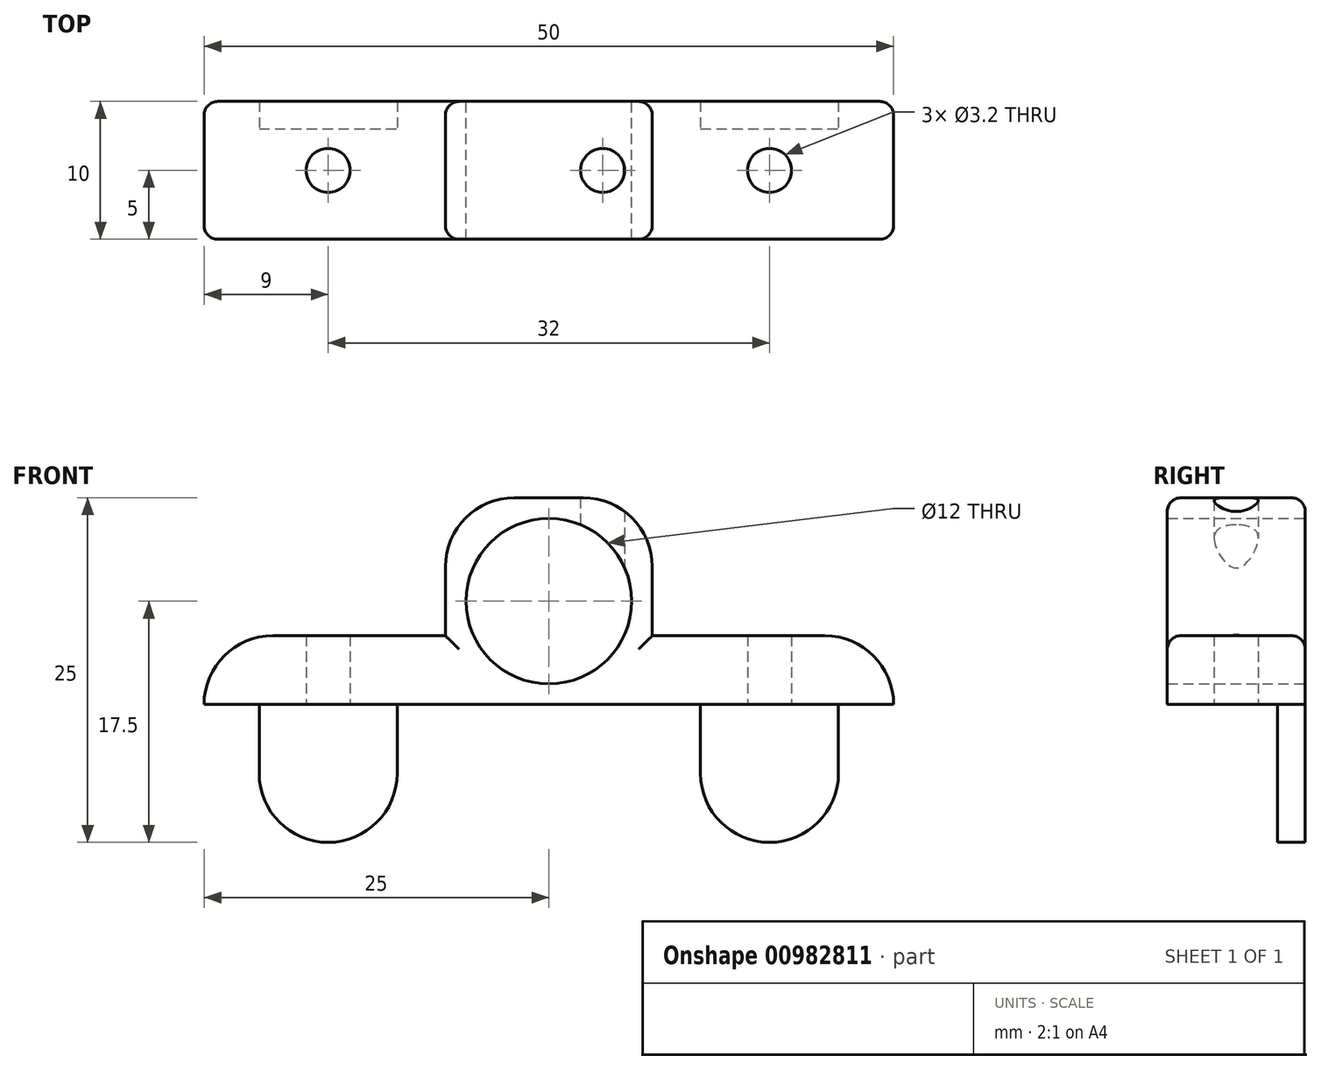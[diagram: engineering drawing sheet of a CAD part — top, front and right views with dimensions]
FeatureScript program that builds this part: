
annotation { "Feature Type Name" : "Feature", "Feature Type Description" : "" }
export const myFeature = defineFeature(function(context is Context, id is Id, definition is map)
    precondition{}
    {
        {
            var Q0;
            Q0=qCreatedBy(makeId("Top.planeOp"),FACE);
            var sketch = newSketch(context, id + "F0", { "sketchPlane" : qUnion([Q0])});
            skLineSegment(sketch, "E0.bottom", {"start": v(25, -5) * mm, "end": v(-25, -5) * mm});
            skLineSegment(sketch, "E0.top", {"start": v(25, 5) * mm, "end": v(-25, 5) * mm});
            skLineSegment(sketch, "E0.left", {"start": v(25, -5) * mm, "end": v(25, 5) * mm});
            skLineSegment(sketch, "E0.right", {"start": v(-25, -5) * mm, "end": v(-25, 5) * mm});
            skPoint(sketch, "E0.middle", {"position": v(0, 0) * mm});
            skCircle(sketch, "E1", {"center": v(-16, 0) * mm, "radius": 1.6 * mm});
            skLineSegment(sketch, "E2", {"start": v(-16, 0) * mm, "end": v(0, 0) * mm, "construction": true});
            skLineSegment(sketch, "E3", {"start": v(0, 5) * mm, "end": v(0, -5) * mm, "construction": true});
            skCircle(sketch, "E4.MirrorC", {"center": v(16, 0) * mm, "radius": 1.6 * mm});
            skSolve(sketch);
        }
        {
            var Q0;
            Q0=makeQuery(id+"F0.imprint","IMPRINT",FACE,{"disambiguationData":[TD([[makeQuery(id+"F0.imprint","IMPRINT",EDGE,{"derivedFrom":sQuery(id+"F0.wireOp",EDGE,"E0.bottom")}),-1.0]])]});
            extrude(context, id + "F1", {"entities" : qUnion([Q0]), "depth" : 5 * mm, "offsetDistance" : 25 * mm});
        }
        {
            var Q0;
            Q0=makeQuery(id+"F1.opExtrude","CAP_FACE",FACE,{"disambiguationData":[OSD([sQuery(id+"F0.wireOp",EDGE,"E0.bottom"),sQuery(id+"F0.wireOp",EDGE,"E0.top"),sQuery(id+"F0.wireOp",EDGE,"E0.left"),sQuery(id+"F0.wireOp",EDGE,"E0.right"),sQuery(id+"F0.wireOp",EDGE,"E1"),sQuery(id+"F0.wireOp",EDGE,"E4.MirrorC")])],"isStart":false});
            var sketch = newSketch(context, id + "F2", { "sketchPlane" : qUnion([Q0])});
            skLineSegment(sketch, "E5.bottom", {"start": v(7.5, -5) * mm, "end": v(-7.5, -5) * mm});
            skLineSegment(sketch, "E5.top", {"start": v(7.5, 5) * mm, "end": v(-7.5, 5) * mm});
            skLineSegment(sketch, "E5.left", {"start": v(7.5, -5) * mm, "end": v(7.5, 5) * mm});
            skLineSegment(sketch, "E5.right", {"start": v(-7.5, -5) * mm, "end": v(-7.5, 5) * mm});
            skPoint(sketch, "E5.middle", {"position": v(0, 0) * mm});
            skCircle(sketch, "E6", {"center": v(-3.9, 0) * mm, "radius": 1.6 * mm});
            skPoint(sketch, "E6.centerSnap0", {"position": v(-7.5, 0) * mm});
            skLineSegment(sketch, "E7", {"start": v(-7.5, 0) * mm, "end": v(-5.5, 0) * mm, "construction": true});
            skCircle(sketch, "E8.MirrorC", {"center": v(3.9, 0) * mm, "radius": 1.6 * mm});
            skSolve(sketch);
        }
        {
            var Q0;
            Q0=makeQuery(id+"F2.imprint","IMPRINT",FACE,{"disambiguationData":[TD([[makeQuery(id+"F2.imprint","IMPRINT",EDGE,{"derivedFrom":sQuery(id+"F2.wireOp",EDGE,"E5.bottom")}),-1.0]])]});
            var Q1;
            Q1=makeQuery(id+"F2.imprint","IMPRINT",FACE,{"disambiguationData":[TD([[makeQuery(id+"F2.imprint","IMPRINT",EDGE,{"derivedFrom":sQuery(id+"F2.wireOp",EDGE,"E8.MirrorC")}),-1.0]])]});
            var Q2;
            Q2=makeQuery(id+"F2.imprint","IMPRINT",FACE,{"disambiguationData":[TD([[makeQuery(id+"F2.imprint","IMPRINT",EDGE,{"derivedFrom":sQuery(id+"F2.wireOp",EDGE,"E6")}),1.0]])]});
            extrude(context, id + "F3", {"entities" : qUnion([Q0, Q1, Q2]), "operationType" : NewBodyOperationType.ADD, "depth" : 10 * mm, "offsetDistance" : 25 * mm});
        }
        {
            var Q0;
            Q0=makeQuery(id+"F3.boolean.opBoolean","MERGE",FACE,{"derivedFrom":[makeQuery(id+"F1.opExtrude","SWEPT_FACE",FACE,{"disambiguationData":[OSD([sQuery(id+"F0.wireOp",EDGE,"E0.top")])]}),makeQuery(id+"F3.opExtrude","SWEPT_FACE",FACE,{"disambiguationData":[OSD([sQuery(id+"F2.wireOp",EDGE,"E5.top")])]})]});
            var sketch = newSketch(context, id + "F4", { "sketchPlane" : qUnion([Q0])});
            skCircle(sketch, "E9", {"center": v(0, 7.5) * mm, "radius": 6 * mm});
            skLineSegment(sketch, "E10", {"start": v(0, 7.5) * mm, "end": v(0, 0) * mm, "construction": true});
            skSolve(sketch);
        }
        {
            var Q0;
            Q0=makeQuery(id+"F3.opExtrude","CAP_EDGE",EDGE,{"disambiguationData":[OSD([sQuery(id+"F2.wireOp",EDGE,"E5.left")])],"isStart":false});
            var Q1;
            Q1=makeQuery(id+"F3.opExtrude","CAP_EDGE",EDGE,{"disambiguationData":[OSD([sQuery(id+"F2.wireOp",EDGE,"E5.right")])],"isStart":false});
            fillet(context, id + "F5", {"entities" : qUnion([Q0, Q1]), "radius" : 5 * mm, "tangentPropagation" : true, "allowEdgeOverflow" : false});
        }
        {
            var Q0;
            Q0=makeQuery(id+"F1.opExtrude","CAP_EDGE",EDGE,{"disambiguationData":[OSD([sQuery(id+"F0.wireOp",EDGE,"E0.right")])],"isStart":false});
            var Q1;
            Q1=makeQuery(id+"F1.opExtrude","CAP_EDGE",EDGE,{"disambiguationData":[OSD([sQuery(id+"F0.wireOp",EDGE,"E0.left")])],"isStart":false});
            fillet(context, id + "F6", {"entities" : qUnion([Q0, Q1]), "radius" : 5 * mm, "tangentPropagation" : true, "allowEdgeOverflow" : false});
        }
        {
            var Q0;
            Q0=makeQuery(id+"F4.imprint","IMPRINT",FACE,{"disambiguationData":[TD([[makeQuery(id+"F4.imprint","IMPRINT",EDGE,{"derivedFrom":sQuery(id+"F4.wireOp",EDGE,"E9")}),1.0]])]});
            extrude(context, id + "F7", {"entities" : qUnion([Q0]), "operationType" : NewBodyOperationType.REMOVE, "oppositeDirection" : true, "depth" : 25 * mm, "offsetDistance" : 25 * mm});
        }
        {
            var Q0;
            Q0=makeQuery(id+"F6.opFillet","BLEND_EDGE",EDGE,{"blendedFrom":[makeQuery(id+"F1.opExtrude","CAP_EDGE",EDGE,{"disambiguationData":[OSD([sQuery(id+"F0.wireOp",EDGE,"E0.left")])],"isStart":false}),makeQuery(id+"F3.boolean.opBoolean","MERGE",FACE,{"derivedFrom":[makeQuery(id+"F1.opExtrude","SWEPT_FACE",FACE,{"disambiguationData":[OSD([sQuery(id+"F0.wireOp",EDGE,"E0.bottom")])]}),makeQuery(id+"F3.opExtrude","SWEPT_FACE",FACE,{"disambiguationData":[OSD([sQuery(id+"F2.wireOp",EDGE,"E5.bottom")])]})]})],"blendedInto":[makeQuery(id+"F3.boolean.opBoolean","MERGE",FACE,{"derivedFrom":[makeQuery(id+"F1.opExtrude","SWEPT_FACE",FACE,{"disambiguationData":[OSD([sQuery(id+"F0.wireOp",EDGE,"E0.bottom")])]}),makeQuery(id+"F3.opExtrude","SWEPT_FACE",FACE,{"disambiguationData":[OSD([sQuery(id+"F2.wireOp",EDGE,"E5.bottom")])]})]})]});
            var Q1;
            {var subQ0=sQuery(id+"F0.wireOp",EDGE,"E0.left");var subQ1=sQuery(id+"F0.wireOp",EDGE,"E0.bottom");Q1=makeQuery(id+"F3.boolean.opBoolean","SPLIT",EDGE,{"disambiguationData":[TD([makeQuery(id+"F1.opExtrude","SWEPT_FACE",FACE,{"disambiguationData":[OSD([subQ0])]})])],"derivedFrom":makeQuery(id+"F1.opExtrude","CAP_EDGE",EDGE,{"disambiguationData":[OSD([subQ1])],"isStart":false})});}
            var Q2;
            Q2=makeQuery(id+"F3.opExtrude","SWEPT_EDGE",EDGE,{"disambiguationData":[OSD([sQuery(id+"F0.wireOp",EDGE,"E0.bottom"),sQuery(id+"F2.wireOp",EDGE,"E5.bottom"),sQuery(id+"F2.wireOp",EDGE,"E5.left")])]});
            var Q3;
            Q3=makeQuery(id+"F5.opFillet","BLEND_EDGE",EDGE,{"blendedFrom":[makeQuery(id+"F3.opExtrude","CAP_EDGE",EDGE,{"disambiguationData":[OSD([sQuery(id+"F2.wireOp",EDGE,"E5.left")])],"isStart":false}),makeQuery(id+"F3.boolean.opBoolean","MERGE",FACE,{"derivedFrom":[makeQuery(id+"F1.opExtrude","SWEPT_FACE",FACE,{"disambiguationData":[OSD([sQuery(id+"F0.wireOp",EDGE,"E0.bottom")])]}),makeQuery(id+"F3.opExtrude","SWEPT_FACE",FACE,{"disambiguationData":[OSD([sQuery(id+"F2.wireOp",EDGE,"E5.bottom")])]})]})],"blendedInto":[makeQuery(id+"F3.boolean.opBoolean","MERGE",FACE,{"derivedFrom":[makeQuery(id+"F1.opExtrude","SWEPT_FACE",FACE,{"disambiguationData":[OSD([sQuery(id+"F0.wireOp",EDGE,"E0.bottom")])]}),makeQuery(id+"F3.opExtrude","SWEPT_FACE",FACE,{"disambiguationData":[OSD([sQuery(id+"F2.wireOp",EDGE,"E5.bottom")])]})]})]});
            var Q4;
            Q4=makeQuery(id+"F3.opExtrude","CAP_EDGE",EDGE,{"disambiguationData":[OSD([sQuery(id+"F2.wireOp",EDGE,"E5.bottom")])],"isStart":false});
            var Q5;
            Q5=makeQuery(id+"F5.opFillet","BLEND_EDGE",EDGE,{"blendedFrom":[makeQuery(id+"F3.opExtrude","CAP_EDGE",EDGE,{"disambiguationData":[OSD([sQuery(id+"F2.wireOp",EDGE,"E5.right")])],"isStart":false}),makeQuery(id+"F3.boolean.opBoolean","MERGE",FACE,{"derivedFrom":[makeQuery(id+"F1.opExtrude","SWEPT_FACE",FACE,{"disambiguationData":[OSD([sQuery(id+"F0.wireOp",EDGE,"E0.bottom")])]}),makeQuery(id+"F3.opExtrude","SWEPT_FACE",FACE,{"disambiguationData":[OSD([sQuery(id+"F2.wireOp",EDGE,"E5.bottom")])]})]})],"blendedInto":[makeQuery(id+"F3.boolean.opBoolean","MERGE",FACE,{"derivedFrom":[makeQuery(id+"F1.opExtrude","SWEPT_FACE",FACE,{"disambiguationData":[OSD([sQuery(id+"F0.wireOp",EDGE,"E0.bottom")])]}),makeQuery(id+"F3.opExtrude","SWEPT_FACE",FACE,{"disambiguationData":[OSD([sQuery(id+"F2.wireOp",EDGE,"E5.bottom")])]})]})]});
            var Q6;
            Q6=makeQuery(id+"F3.opExtrude","SWEPT_EDGE",EDGE,{"disambiguationData":[OSD([sQuery(id+"F0.wireOp",EDGE,"E0.bottom"),sQuery(id+"F2.wireOp",EDGE,"E5.bottom"),sQuery(id+"F2.wireOp",EDGE,"E5.right")])]});
            var Q7;
            {var subQ0=sQuery(id+"F0.wireOp",EDGE,"E0.right");var subQ1=sQuery(id+"F0.wireOp",EDGE,"E0.bottom");Q7=makeQuery(id+"F3.boolean.opBoolean","SPLIT",EDGE,{"disambiguationData":[TD([makeQuery(id+"F1.opExtrude","SWEPT_FACE",FACE,{"disambiguationData":[OSD([subQ0])]})])],"derivedFrom":makeQuery(id+"F1.opExtrude","CAP_EDGE",EDGE,{"disambiguationData":[OSD([subQ1])],"isStart":false})});}
            var Q8;
            Q8=makeQuery(id+"F6.opFillet","BLEND_EDGE",EDGE,{"blendedFrom":[makeQuery(id+"F1.opExtrude","CAP_EDGE",EDGE,{"disambiguationData":[OSD([sQuery(id+"F0.wireOp",EDGE,"E0.right")])],"isStart":false}),makeQuery(id+"F3.boolean.opBoolean","MERGE",FACE,{"derivedFrom":[makeQuery(id+"F1.opExtrude","SWEPT_FACE",FACE,{"disambiguationData":[OSD([sQuery(id+"F0.wireOp",EDGE,"E0.bottom")])]}),makeQuery(id+"F3.opExtrude","SWEPT_FACE",FACE,{"disambiguationData":[OSD([sQuery(id+"F2.wireOp",EDGE,"E5.bottom")])]})]})],"blendedInto":[makeQuery(id+"F3.boolean.opBoolean","MERGE",FACE,{"derivedFrom":[makeQuery(id+"F1.opExtrude","SWEPT_FACE",FACE,{"disambiguationData":[OSD([sQuery(id+"F0.wireOp",EDGE,"E0.bottom")])]}),makeQuery(id+"F3.opExtrude","SWEPT_FACE",FACE,{"disambiguationData":[OSD([sQuery(id+"F2.wireOp",EDGE,"E5.bottom")])]})]})]});
            var Q9;
            {var subQ0=sQuery(id+"F0.wireOp",EDGE,"E0.right");var subQ1=sQuery(id+"F0.wireOp",EDGE,"E0.top");Q9=makeQuery(id+"F3.boolean.opBoolean","SPLIT",EDGE,{"disambiguationData":[TD([makeQuery(id+"F1.opExtrude","SWEPT_FACE",FACE,{"disambiguationData":[OSD([subQ0])]})])],"derivedFrom":makeQuery(id+"F1.opExtrude","CAP_EDGE",EDGE,{"disambiguationData":[OSD([subQ1])],"isStart":false})});}
            var Q10;
            Q10=makeQuery(id+"F3.opExtrude","CAP_EDGE",EDGE,{"disambiguationData":[OSD([sQuery(id+"F2.wireOp",EDGE,"E5.top")])],"isStart":false});
            var Q11;
            Q11=makeQuery(id+"F5.opFillet","BLEND_EDGE",EDGE,{"blendedFrom":[makeQuery(id+"F3.opExtrude","CAP_EDGE",EDGE,{"disambiguationData":[OSD([sQuery(id+"F2.wireOp",EDGE,"E5.left")])],"isStart":false}),makeQuery(id+"F3.boolean.opBoolean","MERGE",FACE,{"derivedFrom":[makeQuery(id+"F1.opExtrude","SWEPT_FACE",FACE,{"disambiguationData":[OSD([sQuery(id+"F0.wireOp",EDGE,"E0.top")])]}),makeQuery(id+"F3.opExtrude","SWEPT_FACE",FACE,{"disambiguationData":[OSD([sQuery(id+"F2.wireOp",EDGE,"E5.top")])]})]})],"blendedInto":[makeQuery(id+"F3.boolean.opBoolean","MERGE",FACE,{"derivedFrom":[makeQuery(id+"F1.opExtrude","SWEPT_FACE",FACE,{"disambiguationData":[OSD([sQuery(id+"F0.wireOp",EDGE,"E0.top")])]}),makeQuery(id+"F3.opExtrude","SWEPT_FACE",FACE,{"disambiguationData":[OSD([sQuery(id+"F2.wireOp",EDGE,"E5.top")])]})]})]});
            var Q12;
            {var subQ0=sQuery(id+"F0.wireOp",EDGE,"E0.left");var subQ1=sQuery(id+"F0.wireOp",EDGE,"E0.top");Q12=makeQuery(id+"F3.boolean.opBoolean","SPLIT",EDGE,{"disambiguationData":[TD([makeQuery(id+"F1.opExtrude","SWEPT_FACE",FACE,{"disambiguationData":[OSD([subQ0])]})])],"derivedFrom":makeQuery(id+"F1.opExtrude","CAP_EDGE",EDGE,{"disambiguationData":[OSD([subQ1])],"isStart":false})});}
            var Q13;
            Q13=makeQuery(id+"F6.opFillet","BLEND_EDGE",EDGE,{"blendedFrom":[makeQuery(id+"F1.opExtrude","CAP_EDGE",EDGE,{"disambiguationData":[OSD([sQuery(id+"F0.wireOp",EDGE,"E0.left")])],"isStart":false}),makeQuery(id+"F3.boolean.opBoolean","MERGE",FACE,{"derivedFrom":[makeQuery(id+"F1.opExtrude","SWEPT_FACE",FACE,{"disambiguationData":[OSD([sQuery(id+"F0.wireOp",EDGE,"E0.top")])]}),makeQuery(id+"F3.opExtrude","SWEPT_FACE",FACE,{"disambiguationData":[OSD([sQuery(id+"F2.wireOp",EDGE,"E5.top")])]})]})],"blendedInto":[makeQuery(id+"F3.boolean.opBoolean","MERGE",FACE,{"derivedFrom":[makeQuery(id+"F1.opExtrude","SWEPT_FACE",FACE,{"disambiguationData":[OSD([sQuery(id+"F0.wireOp",EDGE,"E0.top")])]}),makeQuery(id+"F3.opExtrude","SWEPT_FACE",FACE,{"disambiguationData":[OSD([sQuery(id+"F2.wireOp",EDGE,"E5.top")])]})]})]});
            var Q14;
            Q14=makeQuery(id+"F3.opExtrude","SWEPT_EDGE",EDGE,{"disambiguationData":[OSD([sQuery(id+"F0.wireOp",EDGE,"E0.top"),sQuery(id+"F2.wireOp",EDGE,"E5.top"),sQuery(id+"F2.wireOp",EDGE,"E5.left")])]});
            var Q15;
            Q15=makeQuery(id+"F5.opFillet","BLEND_EDGE",EDGE,{"blendedFrom":[makeQuery(id+"F3.opExtrude","CAP_EDGE",EDGE,{"disambiguationData":[OSD([sQuery(id+"F2.wireOp",EDGE,"E5.right")])],"isStart":false}),makeQuery(id+"F3.boolean.opBoolean","MERGE",FACE,{"derivedFrom":[makeQuery(id+"F1.opExtrude","SWEPT_FACE",FACE,{"disambiguationData":[OSD([sQuery(id+"F0.wireOp",EDGE,"E0.top")])]}),makeQuery(id+"F3.opExtrude","SWEPT_FACE",FACE,{"disambiguationData":[OSD([sQuery(id+"F2.wireOp",EDGE,"E5.top")])]})]})],"blendedInto":[makeQuery(id+"F3.boolean.opBoolean","MERGE",FACE,{"derivedFrom":[makeQuery(id+"F1.opExtrude","SWEPT_FACE",FACE,{"disambiguationData":[OSD([sQuery(id+"F0.wireOp",EDGE,"E0.top")])]}),makeQuery(id+"F3.opExtrude","SWEPT_FACE",FACE,{"disambiguationData":[OSD([sQuery(id+"F2.wireOp",EDGE,"E5.top")])]})]})]});
            var Q16;
            Q16=makeQuery(id+"F3.opExtrude","SWEPT_EDGE",EDGE,{"disambiguationData":[OSD([sQuery(id+"F0.wireOp",EDGE,"E0.top"),sQuery(id+"F2.wireOp",EDGE,"E5.top"),sQuery(id+"F2.wireOp",EDGE,"E5.right")])]});
            var Q17;
            Q17=makeQuery(id+"F6.opFillet","BLEND_EDGE",EDGE,{"blendedFrom":[makeQuery(id+"F1.opExtrude","CAP_EDGE",EDGE,{"disambiguationData":[OSD([sQuery(id+"F0.wireOp",EDGE,"E0.right")])],"isStart":false}),makeQuery(id+"F3.boolean.opBoolean","MERGE",FACE,{"derivedFrom":[makeQuery(id+"F1.opExtrude","SWEPT_FACE",FACE,{"disambiguationData":[OSD([sQuery(id+"F0.wireOp",EDGE,"E0.top")])]}),makeQuery(id+"F3.opExtrude","SWEPT_FACE",FACE,{"disambiguationData":[OSD([sQuery(id+"F2.wireOp",EDGE,"E5.top")])]})]})],"blendedInto":[makeQuery(id+"F3.boolean.opBoolean","MERGE",FACE,{"derivedFrom":[makeQuery(id+"F1.opExtrude","SWEPT_FACE",FACE,{"disambiguationData":[OSD([sQuery(id+"F0.wireOp",EDGE,"E0.top")])]}),makeQuery(id+"F3.opExtrude","SWEPT_FACE",FACE,{"disambiguationData":[OSD([sQuery(id+"F2.wireOp",EDGE,"E5.top")])]})]})]});
            fillet(context, id + "F8", {"entities" : qUnion([Q0, Q1, Q2, Q3, Q4, Q5, Q6, Q7, Q8, Q9, Q10, Q11, Q12, Q13, Q14, Q15, Q16, Q17]), "radius" : 1 * mm, "tangentPropagation" : true, "allowEdgeOverflow" : false});
        }
        {
            var Q0;
            Q0=makeQuery(id+"F1.opExtrude","CAP_FACE",FACE,{"disambiguationData":[OSD([sQuery(id+"F0.wireOp",EDGE,"E0.bottom"),sQuery(id+"F0.wireOp",EDGE,"E0.top"),sQuery(id+"F0.wireOp",EDGE,"E0.left"),sQuery(id+"F0.wireOp",EDGE,"E0.right"),sQuery(id+"F0.wireOp",EDGE,"E1"),sQuery(id+"F0.wireOp",EDGE,"E4.MirrorC")])],"isStart":true});
            var sketch = newSketch(context, id + "F9", { "sketchPlane" : qUnion([Q0])});
            skLineSegment(sketch, "E11.bottom", {"start": v(-25, -3) * mm, "end": v(25, -3) * mm, "construction": true});
            skLineSegment(sketch, "E11.top", {"start": v(-25, 3) * mm, "end": v(25, 3) * mm, "construction": true});
            skLineSegment(sketch, "E11.left", {"start": v(-25, -3) * mm, "end": v(-25, 3) * mm, "construction": true});
            skLineSegment(sketch, "E11.right", {"start": v(25, -3) * mm, "end": v(25, 3) * mm, "construction": true});
            skLineSegment(sketch, "E12", {"start": v(0, 0) * mm, "end": v(0, -3) * mm, "construction": true});
            skLineSegment(sketch, "E13.bottom", {"start": v(-21, -5) * mm, "end": v(-11, -5) * mm});
            skLineSegment(sketch, "E13.top", {"start": v(-21, -3) * mm, "end": v(-11, -3) * mm});
            skLineSegment(sketch, "E13.left", {"start": v(-21, -5) * mm, "end": v(-21, -3) * mm});
            skLineSegment(sketch, "E13.right", {"start": v(-11, -5) * mm, "end": v(-11, -3) * mm});
            skLineSegment(sketch, "E14", {"start": v(-16, 0) * mm, "end": v(-16, -3) * mm, "construction": true});
            skLineSegment(sketch, "E15.MirrorCS", {"start": v(21, -5) * mm, "end": v(21, -3) * mm});
            skLineSegment(sketch, "E16.MirrorCS", {"start": v(11, -5) * mm, "end": v(11, -3) * mm});
            skLineSegment(sketch, "E17.MirrorCS", {"start": v(21, -5) * mm, "end": v(11, -5) * mm});
            skLineSegment(sketch, "E18", {"start": v(11, -3) * mm, "end": v(21, -3) * mm});
            skPoint(sketch, "E19", {"position": v(-8.9, 0) * mm});
            skCircle(sketch, "E20.cCircle", {"center": v(-8.9, 0) * mm, "radius": 3.1 * mm, "construction": true});
            skLineSegment(sketch, "E20.0", {"start": v(-5.8, 0) * mm, "end": v(-7.35, -2.68) * mm});
            skLineSegment(sketch, "E20.1", {"start": v(-7.35, -2.68) * mm, "end": v(-10.45, -2.68) * mm});
            skLineSegment(sketch, "E20.2", {"start": v(-10.45, -2.68) * mm, "end": v(-12, 0) * mm});
            skLineSegment(sketch, "E20.3", {"start": v(-12, 0) * mm, "end": v(-10.45, 2.68) * mm});
            skLineSegment(sketch, "E20.4", {"start": v(-10.45, 2.68) * mm, "end": v(-7.35, 2.68) * mm});
            skLineSegment(sketch, "E20.5", {"start": v(-7.35, 2.68) * mm, "end": v(-5.8, 0) * mm});
            skLineSegment(sketch, "E21.MirrorCS", {"start": v(12, 0) * mm, "end": v(10.45, 2.68) * mm});
            skLineSegment(sketch, "E22.MirrorCS", {"start": v(10.45, -2.68) * mm, "end": v(12, 0) * mm});
            skLineSegment(sketch, "E23.MirrorCS", {"start": v(7.35, -2.68) * mm, "end": v(10.45, -2.68) * mm});
            skLineSegment(sketch, "E24.MirrorCS", {"start": v(5.8, 0) * mm, "end": v(7.35, -2.68) * mm});
            skLineSegment(sketch, "E25.MirrorCS", {"start": v(7.35, 2.68) * mm, "end": v(5.8, 0) * mm});
            skLineSegment(sketch, "E26.MirrorCS", {"start": v(10.45, 2.68) * mm, "end": v(7.35, 2.68) * mm});
            skSolve(sketch);
        }
        {
            var Q0;
            Q0=makeQuery(id+"F9.imprint","IMPRINT",FACE,{"disambiguationData":[TD([[makeQuery(id+"F9.imprint","IMPRINT",EDGE,{"derivedFrom":sQuery(id+"F9.wireOp",EDGE,"E13.bottom")}),-1.0]])]});
            var Q1;
            Q1=makeQuery(id+"F9.imprint","IMPRINT",FACE,{"disambiguationData":[TD([[makeQuery(id+"F9.imprint","IMPRINT",EDGE,{"derivedFrom":sQuery(id+"F9.wireOp",EDGE,"E15.MirrorCS")}),1.0]])]});
            extrude(context, id + "F10", {"entities" : qUnion([Q0, Q1]), "operationType" : NewBodyOperationType.ADD, "depth" : 10 * mm, "offsetDistance" : 25 * mm});
        }
        {
            var Q0;
            Q0=makeQuery(id+"F10.opExtrude","CAP_EDGE",EDGE,{"disambiguationData":[OSD([sQuery(id+"F9.wireOp",EDGE,"E16.MirrorCS")])],"isStart":false});
            var Q1;
            Q1=makeQuery(id+"F10.opExtrude","CAP_EDGE",EDGE,{"disambiguationData":[OSD([sQuery(id+"F9.wireOp",EDGE,"E15.MirrorCS")])],"isStart":false});
            var Q2;
            Q2=makeQuery(id+"F10.opExtrude","CAP_EDGE",EDGE,{"disambiguationData":[OSD([sQuery(id+"F9.wireOp",EDGE,"E13.left")])],"isStart":false});
            var Q3;
            Q3=makeQuery(id+"F10.opExtrude","CAP_EDGE",EDGE,{"disambiguationData":[OSD([sQuery(id+"F9.wireOp",EDGE,"E13.right")])],"isStart":false});
            fillet(context, id + "F11", {"entities" : qUnion([Q0, Q1, Q2, Q3]), "radius" : 5 * mm, "tangentPropagation" : true, "allowEdgeOverflow" : false});
        }
        {
            var Q0;
            Q0=qCreatedBy(makeId("Top.planeOp"),FACE);
            cPlane(context, id + "F12", {"entities" : qUnion([Q0]), "cplaneType" : CPlaneType.OFFSET, "offset" : 7.5 * mm, "width" : 150 * mm, "height" : 150 * mm});
        }
    });
